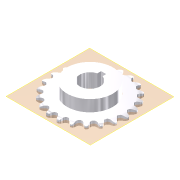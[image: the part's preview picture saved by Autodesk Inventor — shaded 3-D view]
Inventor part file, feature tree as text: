
AUTODESK INVENTOR PART (.ipt)
format: ipt  version: 2011 (Build 150239000, 239)  size: 640,512 bytes
history: native  units: mm
features: other x6, extrude x4, sketch x2, pattern_linear x1, pattern_circular x1
ambient origin geometry x8: Origin, YZ Plane, XZ Plane, XY Plane, X Axis, Y Axis, Z Axis, Center Point
bodies: Solid1 (feature_tree)
feature tree (14):
  other  "Theoretical Tooth Profile"
  other  "Tooth Profile"
  other  "Section Profile"
  other  "Shroud"
  other  "Strand"
  pattern_linear  "Strand Pattern"  Spacing1=1.697355mm  [1 undecoded]
  extrude  "Theoretical Tooth"  Depth=22.292615mm
  extrude  "Tooth"  Depth=2.697327mm
  pattern_circular  "Tooth Pattern"  [2 undecoded]
  other  "Timing Plane"
  extrude  "Extrusion4"  Depth=4.338955mm
  extrude  "Extrusion5"  Depth=4.6228mm
  sketch  "Sketch4"  dims[d0=44.619381mm]
  sketch  "Sketch5"  dims[d2=2.855993mm d3=1.697355mm d10=22.292615mm d11=2.697327mm d12=2.6416mm d13=4.338955mm d14=4.6228mm d18=10.0mm d19=0.0mm d20=220.0mm d21=360.0deg d23=1.905mm d28=0.0mm d29=0.0mm d30=3.1242mm d31=36.54522mm d32=3.1242mm d33=0.79375mm d34=6.75005mm d36=90.0deg d37=90.0deg d38=10.0mm d40=6.4008mm d42=0.0mm d43=1.5621mm d44=23.720612mm d45=1.697355mm d46=9.50976mm d47=0.0mm d48=25.4mm d49=0.0mm d50=10.0mm d51=12.7mm d52=28.575mm d53=7.1628mm d54=0.0mm d55=12.7508mm d56=3.175mm d57=2.38125mm d58=5.1308mm d59=0.0mm]
note: 3 required parameter values undecoded (feature->parameter linkage not recoverable at this tier; creation-order binding heuristic only, values carry confidence <= 0.55)
